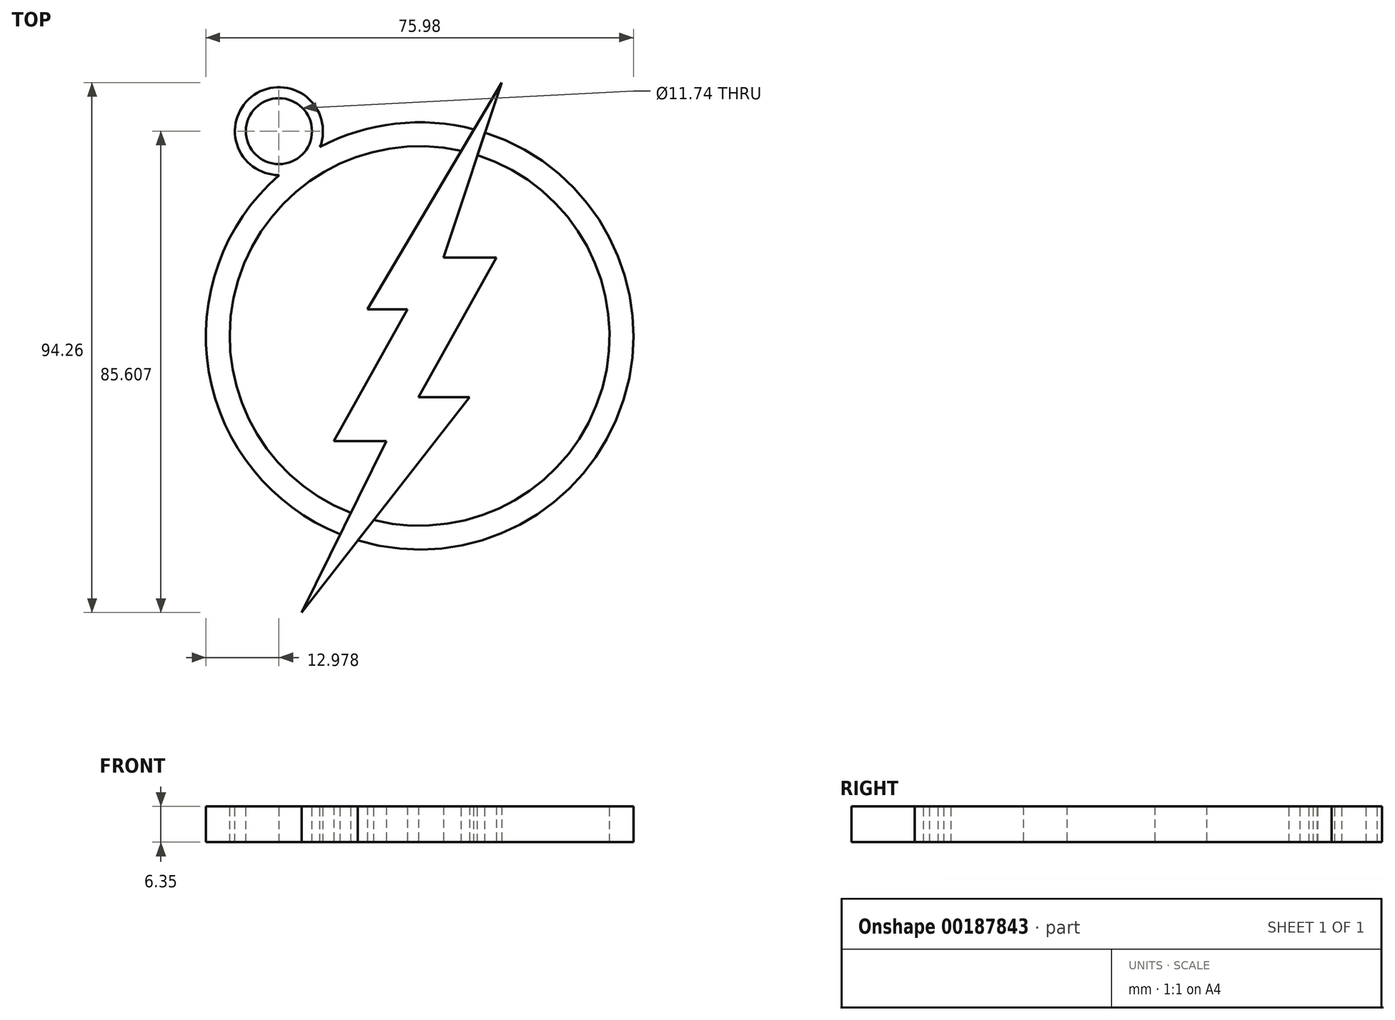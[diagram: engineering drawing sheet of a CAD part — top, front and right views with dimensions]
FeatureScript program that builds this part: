
annotation { "Feature Type Name" : "Feature", "Feature Type Description" : "" }
export const myFeature = defineFeature(function(context is Context, id is Id, definition is map)
    precondition{}
    {
        {
            var Q0;
            Q0=qCreatedBy(makeId("Top.planeOp"),FACE);
            var sketch = newSketch(context, id + "F0", { "sketchPlane" : qUnion([Q0])});
            skLineSegment(sketch, "E0", {"start": v(20.53, 51.39) * mm, "end": v(-3.33, 11.02) * mm});
            skLineSegment(sketch, "E1", {"start": v(-3.33, 11.02) * mm, "end": v(3.78, 11.02) * mm});
            skLineSegment(sketch, "E2", {"start": v(3.78, 11.02) * mm, "end": v(-9.3, -12.37) * mm});
            skLineSegment(sketch, "E3", {"start": v(-9.3, -12.37) * mm, "end": v(0, -12.37) * mm});
            skLineSegment(sketch, "E4", {"start": v(0, -12.37) * mm, "end": v(-15.02, -42.87) * mm});
            skLineSegment(sketch, "E5", {"start": v(-15.02, -42.87) * mm, "end": v(14.8, -4.57) * mm});
            skLineSegment(sketch, "E6", {"start": v(14.8, -4.57) * mm, "end": v(5.75, -4.57) * mm});
            skLineSegment(sketch, "E7", {"start": v(5.75, -4.57) * mm, "end": v(19.61, 20.24) * mm});
            skLineSegment(sketch, "E8", {"start": v(19.61, 20.24) * mm, "end": v(10.2, 20.24) * mm});
            skLineSegment(sketch, "E9", {"start": v(20.53, 51.39) * mm, "end": v(10.2, 20.24) * mm});
            skSolve(sketch);
        }
        {
            var Q0;
            Q0=qSketchRegion(id+"F0",true);
            extrude(context, id + "F1", {"entities" : qUnion([Q0]), "depth" : 6.35 * mm});
        }
        {
            var Q0;
            Q0=makeQuery(id+"F1.opExtrude","CAP_FACE",FACE,{"disambiguationData":[OSD([sQuery(id+"F0.wireOp",EDGE,"E0"),sQuery(id+"F0.wireOp",EDGE,"E1"),sQuery(id+"F0.wireOp",EDGE,"E2"),sQuery(id+"F0.wireOp",EDGE,"E3"),sQuery(id+"F0.wireOp",EDGE,"E4"),sQuery(id+"F0.wireOp",EDGE,"E5"),sQuery(id+"F0.wireOp",EDGE,"E6"),sQuery(id+"F0.wireOp",EDGE,"E7"),sQuery(id+"F0.wireOp",EDGE,"E8"),sQuery(id+"F0.wireOp",EDGE,"E9")])],"isStart":false});
            var sketch = newSketch(context, id + "F2", { "sketchPlane" : qUnion([Q0])});
            skCircle(sketch, "E10", {"center": v(5.95, 6.31) * mm, "radius": 33.75 * mm});
            skCircle(sketch, "E11", {"center": v(5.95, 6.31) * mm, "radius": 38 * mm});
            skSolve(sketch);
        }
        {
            var Q0;
            {var subQ0=sQuery(id+"F2.wireOp",EDGE,"E10");var subQ1=makeQuery(id+"F1.opExtrude","CAP_EDGE",EDGE,{"disambiguationData":[OSD([sQuery(id+"F0.wireOp",EDGE,"E0")])],"isStart":false});var subQ2=makeQuery(id+"F2.imprint","INTERSECT",VERTEX,{"derivedFrom":[subQ1,subQ0]});Q0=makeQuery(id+"F2.imprint","IMPRINT",FACE,{"disambiguationData":[TD([[makeQuery(id+"F2.imprint","IMPRINT",EDGE,{"disambiguationData":[TD([[subQ2,-1.0]])],"derivedFrom":subQ0}),-1.0]])]});}
            var Q1;
            {var subQ0=sQuery(id+"F2.wireOp",EDGE,"E10");var subQ1=makeQuery(id+"F1.opExtrude","CAP_EDGE",EDGE,{"disambiguationData":[OSD([sQuery(id+"F0.wireOp",EDGE,"E9")])],"isStart":false});var subQ2=makeQuery(id+"F2.imprint","INTERSECT",VERTEX,{"derivedFrom":[subQ1,subQ0]});Q1=makeQuery(id+"F2.imprint","IMPRINT",FACE,{"disambiguationData":[TD([[makeQuery(id+"F2.imprint","IMPRINT",EDGE,{"disambiguationData":[TD([[subQ2,1.0]])],"derivedFrom":subQ0}),-1.0]])]});}
            extrude(context, id + "F3", {"entities" : qUnion([Q0, Q1]), "oppositeDirection" : true, "depth" : 6.35 * mm});
        }
        {
            var Q0;
            Q0=makeQuery(id+"F1.opExtrude","CAP_FACE",FACE,{"disambiguationData":[OSD([sQuery(id+"F0.wireOp",EDGE,"E0"),sQuery(id+"F0.wireOp",EDGE,"E1"),sQuery(id+"F0.wireOp",EDGE,"E2"),sQuery(id+"F0.wireOp",EDGE,"E3"),sQuery(id+"F0.wireOp",EDGE,"E4"),sQuery(id+"F0.wireOp",EDGE,"E5"),sQuery(id+"F0.wireOp",EDGE,"E6"),sQuery(id+"F0.wireOp",EDGE,"E7"),sQuery(id+"F0.wireOp",EDGE,"E8"),sQuery(id+"F0.wireOp",EDGE,"E9")])],"isStart":false});
            var sketch = newSketch(context, id + "F4", { "sketchPlane" : qUnion([Q0])});
            skCircle(sketch, "E12", {"center": v(-19.06, 42.74) * mm, "radius": 7.82 * mm});
            skCircle(sketch, "E13", {"center": v(-19.06, 42.74) * mm, "radius": 5.87 * mm});
            skSolve(sketch);
        }
        {
            var Q0;
            Q0=qSketchRegion(id+"F4",true);
            extrude(context, id + "F5", {"entities" : qUnion([Q0]), "operationType" : NewBodyOperationType.ADD, "oppositeDirection" : true, "depth" : 6.35 * mm});
        }
    });
